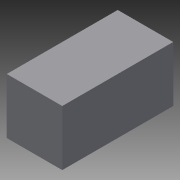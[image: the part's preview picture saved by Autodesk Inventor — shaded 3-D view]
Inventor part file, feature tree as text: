
AUTODESK INVENTOR PART (.ipt)
format: ipt  version: 2014 (Build 180170000, 170)  size: 68,608 bytes
history: native  units: in
note: dims shown in document units (in); Inventor stores cm internally (conversion verified against a paired STEP export)
features: extrude x1, sketch x1
ambient origin geometry x8: Origin, YZ Plane, XZ Plane, XY Plane, X Axis, Y Axis, Z Axis, Center Point
bodies: Solid1 (feature_tree)
feature tree (2):
  extrude  "Extrusion1"  Depth=72.0in
  sketch  "Sketch1"  dims[d0=36.0in d1=72.0in d2=36.0in d3=0.0in]
